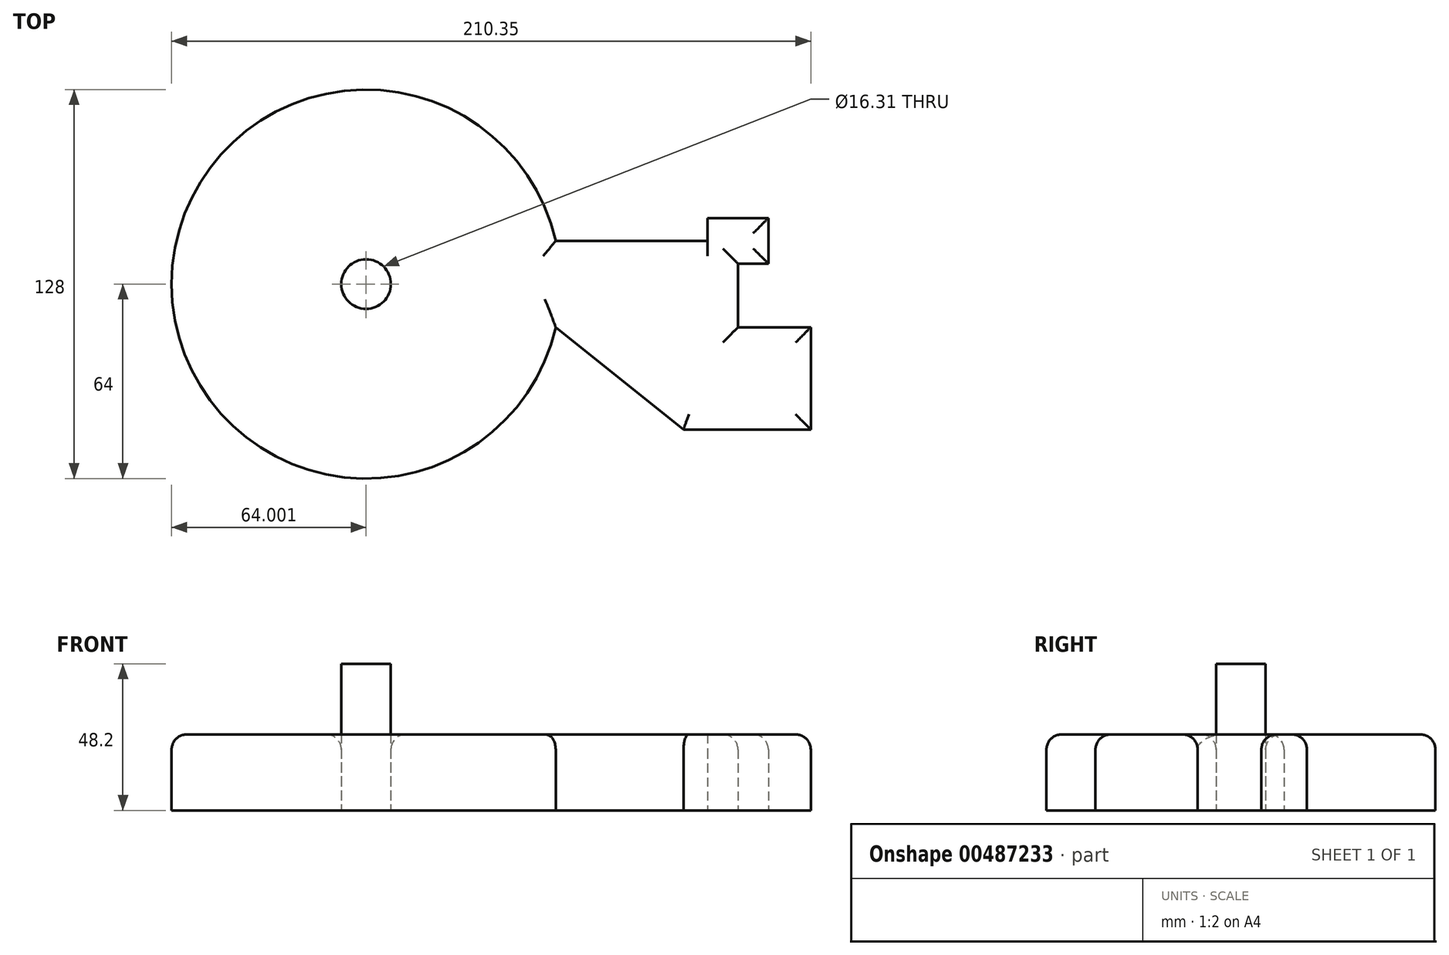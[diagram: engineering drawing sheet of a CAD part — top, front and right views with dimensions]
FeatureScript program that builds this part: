
annotation { "Feature Type Name" : "Feature", "Feature Type Description" : "" }
export const myFeature = defineFeature(function(context is Context, id is Id, definition is map)
    precondition{}
    {
        {
            var Q0;
            Q0=qCreatedBy(makeId("Top.planeOp"),FACE);
            var sketch = newSketch(context, id + "F0", { "sketchPlane" : qUnion([Q0])});
            skLineSegment(sketch, "E0.bottom", {"start": v(30, -14.22) * mm, "end": v(-30, -14.22) * mm});
            skLineSegment(sketch, "E0.top", {"start": v(30, 14.22) * mm, "end": v(-30, 14.22) * mm});
            skLineSegment(sketch, "E0.left", {"start": v(30, -14.22) * mm, "end": v(30, 14.22) * mm});
            skLineSegment(sketch, "E0.right", {"start": v(-30, -14.22) * mm, "end": v(-30, 14.22) * mm});
            skPoint(sketch, "E0.middle", {"position": v(0, 0) * mm});
            skLineSegment(sketch, "E1.bottom", {"start": v(40, 6.72) * mm, "end": v(20, 6.72) * mm});
            skLineSegment(sketch, "E1.top", {"start": v(40, 21.72) * mm, "end": v(20, 21.72) * mm});
            skLineSegment(sketch, "E1.left", {"start": v(40, 6.72) * mm, "end": v(40, 21.72) * mm});
            skLineSegment(sketch, "E1.right", {"start": v(20, 6.72) * mm, "end": v(20, 21.72) * mm});
            skPoint(sketch, "E1.middle", {"position": v(30, 14.22) * mm});
            skArc(sketch, "E2", {"start": v(-30, 14.22) * mm, "mid": v(-156.4, 0) * mm, "end": v(-30, -14.22) * mm});
            skLineSegment(sketch, "E3", {"start": v(-30, -14.22) * mm, "end": v(12.06, -47.86) * mm});
            skLineSegment(sketch, "E4", {"start": v(12.06, -47.86) * mm, "end": v(53.95, -47.86) * mm});
            skLineSegment(sketch, "E5", {"start": v(53.95, -47.86) * mm, "end": v(53.95, -14.22) * mm});
            skLineSegment(sketch, "E6", {"start": v(53.95, -14.22) * mm, "end": v(30, -14.22) * mm});
            skFitSpline(sketch, "E7", {"points": [v(20, 21.72) * mm, v(18.02, 16.76) * mm, v(15.84, 17.34) * mm, v(11.54, 15.73) * mm, v(4.55, 14.22) * mm], "startDerivative": vector(-22.75, -20.48) * mm, "endDerivative": vector(-23.7, 0) * mm});
            skCircle(sketch, "E8", {"center": v(-92.4, 0) * mm, "radius": 8.15 * mm});
            skSolve(sketch);
        }
        {
            var Q0;
            Q0=makeQuery(id+"F0.imprint","IMPRINT",FACE,{"disambiguationData":[TD([[makeQuery(id+"F0.imprint","IMPRINT",EDGE,{"derivedFrom":sQuery(id+"F0.wireOp",EDGE,"E0.right")}),1.0]])]});
            var Q1;
            {var subQ1=sQuery(id+"F0.wireOp",EDGE,"E0.bottom");Q1=makeQuery(id+"F0.imprint","IMPRINT",FACE,{"disambiguationData":[TD([[makeQuery(id+"F0.imprint","IMPRINT",EDGE,{"derivedFrom":subQ1}),-1.0]])]});}
            var Q2;
            Q2=makeQuery(id+"F0.imprint","IMPRINT",FACE,{"disambiguationData":[TD([[makeQuery(id+"F0.imprint","IMPRINT",EDGE,{"derivedFrom":sQuery(id+"F0.wireOp",EDGE,"E0.bottom")}),1.0]])]});
            var Q3;
            {var subQ0=sQuery(id+"F0.wireOp",EDGE,"E1.top");Q3=makeQuery(id+"F0.imprint","IMPRINT",FACE,{"disambiguationData":[TD([[makeQuery(id+"F0.imprint","IMPRINT",EDGE,{"derivedFrom":subQ0}),1.0]])]});}
            var Q4;
            {var subQ0=sQuery(id+"F0.wireOp",EDGE,"E0.left");var subQ1=sQuery(id+"F0.wireOp",EDGE,"E0.top");var subQ2=makeQuery(id+"F0.imprint","INTERSECT",VERTEX,{"derivedFrom":[subQ1,subQ0]});Q4=makeQuery(id+"F0.imprint","IMPRINT",FACE,{"disambiguationData":[TD([[makeQuery(id+"F0.imprint","IMPRINT",EDGE,{"disambiguationData":[TD([[subQ2,-1.0]])],"derivedFrom":subQ1}),1.0]])]});}
            extrude(context, id + "F1", {"entities" : qUnion([Q0, Q1, Q2, Q3, Q4]), "depth" : 25 * mm, "offsetDistance" : 25 * mm});
        }
        {
            var Q0;
            Q0=makeQuery(id+"F0.imprint","IMPRINT",FACE,{"disambiguationData":[TD([[makeQuery(id+"F0.imprint","IMPRINT",EDGE,{"derivedFrom":sQuery(id+"F0.wireOp",EDGE,"E8")}),1.0]])]});
            extrude(context, id + "F2", {"entities" : qUnion([Q0]), "depth" : 48.2 * mm, "offsetDistance" : 25 * mm});
        }
        {
            var Q0;
            Q0=makeQuery(id+"F1.opExtrude","CAP_EDGE",EDGE,{"disambiguationData":[OSD([sQuery(id+"F0.wireOp",EDGE,"E3")])],"isStart":false});
            var Q1;
            Q1=makeQuery(id+"F1.opExtrude","CAP_EDGE",EDGE,{"disambiguationData":[OSD([sQuery(id+"F0.wireOp",EDGE,"E4")])],"isStart":false});
            var Q2;
            Q2=makeQuery(id+"F1.opExtrude","CAP_EDGE",EDGE,{"disambiguationData":[OSD([sQuery(id+"F0.wireOp",EDGE,"E6")])],"isStart":false});
            var Q3;
            Q3=makeQuery(id+"F1.opExtrude","CAP_EDGE",EDGE,{"disambiguationData":[OSD([sQuery(id+"F0.wireOp",EDGE,"E5")])],"isStart":false});
            var Q4;
            Q4=makeQuery(id+"F1.opExtrude","CAP_EDGE",EDGE,{"disambiguationData":[OSD([sQuery(id+"F0.wireOp",EDGE,"E2")])],"isStart":false});
            var Q5;
            Q5=makeQuery(id+"F1.opExtrude","CAP_EDGE",EDGE,{"disambiguationData":[OSD([sQuery(id+"F0.wireOp",EDGE,"E0.left")])],"isStart":false});
            var Q6;
            Q6=makeQuery(id+"F1.opExtrude","CAP_EDGE",EDGE,{"disambiguationData":[OSD([sQuery(id+"F0.wireOp",EDGE,"E1.bottom")])],"isStart":false});
            var Q7;
            Q7=makeQuery(id+"F1.opExtrude","CAP_EDGE",EDGE,{"disambiguationData":[OSD([sQuery(id+"F0.wireOp",EDGE,"E1.top")])],"isStart":false});
            var Q8;
            Q8=makeQuery(id+"F1.opExtrude","CAP_EDGE",EDGE,{"disambiguationData":[OSD([sQuery(id+"F0.wireOp",EDGE,"E1.left")])],"isStart":false});
            var Q9;
            Q9=makeQuery(id+"F1.opExtrude","CAP_EDGE",EDGE,{"disambiguationData":[OSD([sQuery(id+"F0.wireOp",EDGE,"E0.top")])],"isStart":false});
            var Q10;
            Q10=makeQuery(id+"F1.opExtrude","CAP_EDGE",EDGE,{"disambiguationData":[OSD([sQuery(id+"F0.wireOp",EDGE,"E8")])],"isStart":false});
            fillet(context, id + "F3", {"entities" : qUnion([Q0, Q1, Q2, Q3, Q4, Q5, Q6, Q7, Q8, Q9, Q10]), "radius" : 5 * mm, "tangentPropagation" : true, "allowEdgeOverflow" : false});
        }
    });
